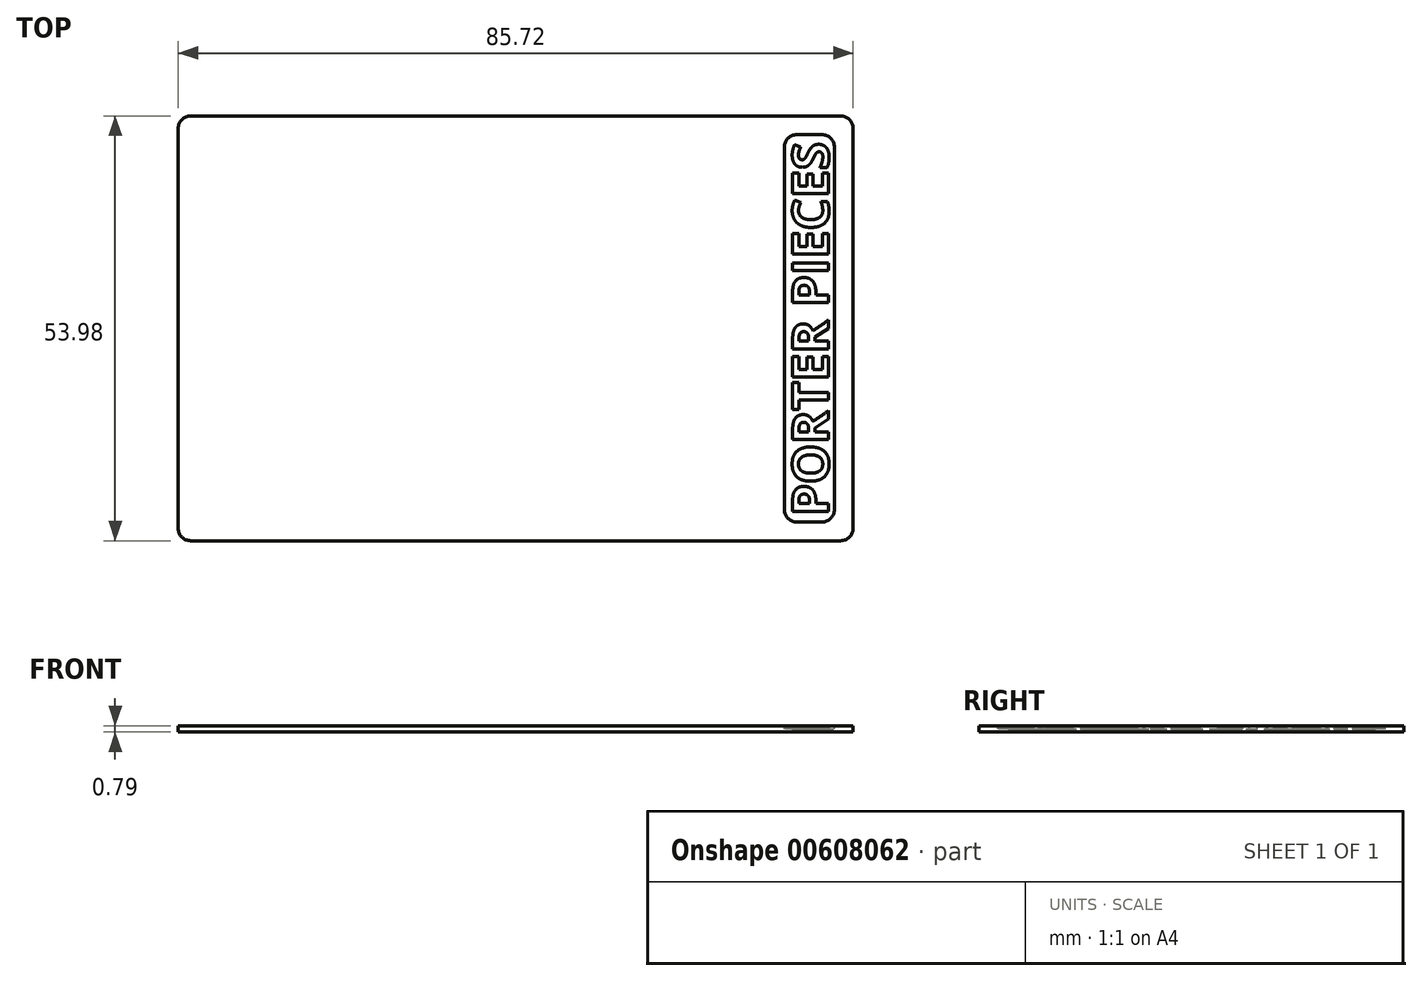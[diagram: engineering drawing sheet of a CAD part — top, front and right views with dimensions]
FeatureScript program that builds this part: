
annotation { "Feature Type Name" : "Feature", "Feature Type Description" : "" }
export const myFeature = defineFeature(function(context is Context, id is Id, definition is map)
    precondition{}
    {
        {
            var Q0;
            Q0=qCreatedBy(makeId("Top.planeOp"),FACE);
            var sketch = newSketch(context, id + "F0", { "sketchPlane" : qUnion([Q0])});
            skLineSegment(sketch, "E0.bottom", {"start": v(42.86, 26.99) * mm, "end": v(-42.86, 26.99) * mm});
            skLineSegment(sketch, "E0.top", {"start": v(42.86, -26.99) * mm, "end": v(-42.86, -26.99) * mm});
            skLineSegment(sketch, "E0.left", {"start": v(42.86, 26.99) * mm, "end": v(42.86, -26.99) * mm});
            skLineSegment(sketch, "E0.right", {"start": v(-42.86, 26.99) * mm, "end": v(-42.86, -26.99) * mm});
            skPoint(sketch, "E0.middle", {"position": v(0, 0) * mm});
            skSolve(sketch);
        }
        {
            var Q0;
            Q0=makeQuery(id+"F0.imprint","IMPRINT",FACE,{"disambiguationData":[TD([[makeQuery(id+"F0.imprint","IMPRINT",EDGE,{"derivedFrom":sQuery(id+"F0.wireOp",EDGE,"E0.bottom")}),1.0]])]});
            extrude(context, id + "F1", {"entities" : qUnion([Q0]), "depth" : 0.8 * mm, "offsetDistance" : 25.4 * mm});
        }
        {
            var Q0;
            Q0=makeQuery(id+"F1.opExtrude","SWEPT_EDGE",EDGE,{"disambiguationData":[OSD([sQuery(id+"F0.wireOp",EDGE,"E0.bottom"),sQuery(id+"F0.wireOp",EDGE,"E0.left")])]});
            var Q1;
            Q1=makeQuery(id+"F1.opExtrude","SWEPT_EDGE",EDGE,{"disambiguationData":[OSD([sQuery(id+"F0.wireOp",EDGE,"E0.bottom"),sQuery(id+"F0.wireOp",EDGE,"E0.right")])]});
            var Q2;
            Q2=makeQuery(id+"F1.opExtrude","SWEPT_EDGE",EDGE,{"disambiguationData":[OSD([sQuery(id+"F0.wireOp",EDGE,"E0.top"),sQuery(id+"F0.wireOp",EDGE,"E0.right")])]});
            var Q3;
            Q3=makeQuery(id+"F1.opExtrude","SWEPT_EDGE",EDGE,{"disambiguationData":[OSD([sQuery(id+"F0.wireOp",EDGE,"E0.top"),sQuery(id+"F0.wireOp",EDGE,"E0.left")])]});
            fillet(context, id + "F2", {"entities" : qUnion([Q0, Q1, Q2, Q3]), "radius" : 1.59 * mm, "tangentPropagation" : true, "allowEdgeOverflow" : false});
        }
        {
            var Q0;
            Q0=makeQuery(id+"F1.opExtrude","CAP_FACE",FACE,{"disambiguationData":[OSD([sQuery(id+"F0.wireOp",EDGE,"E0.bottom"),sQuery(id+"F0.wireOp",EDGE,"E0.top"),sQuery(id+"F0.wireOp",EDGE,"E0.left"),sQuery(id+"F0.wireOp",EDGE,"E0.right")])],"isStart":false});
            var sketch = newSketch(context, id + "F3", { "sketchPlane" : qUnion([Q0])});
            skLineSegment(sketch, "E1.bottom", {"start": v(34.13, -24.6) * mm, "end": v(40.48, -24.6) * mm});
            skLineSegment(sketch, "E1.top", {"start": v(34.13, 24.6) * mm, "end": v(40.48, 24.6) * mm});
            skLineSegment(sketch, "E1.left", {"start": v(34.13, -24.6) * mm, "end": v(34.13, 24.6) * mm});
            skLineSegment(sketch, "E1.right", {"start": v(40.48, -24.6) * mm, "end": v(40.48, 24.6) * mm});
            skSolve(sketch);
        }
        {
            var Q0;
            Q0=makeQuery(id+"F3.imprint","IMPRINT",FACE,{"disambiguationData":[TD([[makeQuery(id+"F3.imprint","IMPRINT",EDGE,{"derivedFrom":sQuery(id+"F3.wireOp",EDGE,"E1.bottom")}),1.0]])]});
            extrude(context, id + "F4", {"entities" : qUnion([Q0]), "operationType" : NewBodyOperationType.REMOVE, "oppositeDirection" : true, "depth" : 0.4 * mm, "offsetDistance" : 25.4 * mm});
        }
        {
            var Q0;
            Q0=makeQuery(id+"F4.boolean.opBoolean","COPY",EDGE,{"derivedFrom":makeQuery(id+"F4.opExtrude","SWEPT_EDGE",EDGE,{"disambiguationData":[OSD([sQuery(id+"F3.wireOp",EDGE,"E1.bottom"),sQuery(id+"F3.wireOp",EDGE,"E1.left")])]})});
            var Q1;
            Q1=makeQuery(id+"F4.boolean.opBoolean","COPY",EDGE,{"derivedFrom":makeQuery(id+"F4.opExtrude","SWEPT_EDGE",EDGE,{"disambiguationData":[OSD([sQuery(id+"F3.wireOp",EDGE,"E1.bottom"),sQuery(id+"F3.wireOp",EDGE,"E1.right")])]})});
            var Q2;
            Q2=makeQuery(id+"F4.boolean.opBoolean","COPY",EDGE,{"derivedFrom":makeQuery(id+"F4.opExtrude","SWEPT_EDGE",EDGE,{"disambiguationData":[OSD([sQuery(id+"F3.wireOp",EDGE,"E1.top"),sQuery(id+"F3.wireOp",EDGE,"E1.right")])]})});
            var Q3;
            Q3=makeQuery(id+"F4.boolean.opBoolean","COPY",EDGE,{"derivedFrom":makeQuery(id+"F4.opExtrude","SWEPT_EDGE",EDGE,{"disambiguationData":[OSD([sQuery(id+"F3.wireOp",EDGE,"E1.top"),sQuery(id+"F3.wireOp",EDGE,"E1.left")])]})});
            fillet(context, id + "F5", {"entities" : qUnion([Q0, Q1, Q2, Q3]), "radius" : 1.59 * mm, "tangentPropagation" : true, "allowEdgeOverflow" : false});
        }
        {
            var Q0;
            Q0=makeQuery(id+"F4.boolean.opBoolean","COPY",FACE,{"derivedFrom":makeQuery(id+"F4.opExtrude","CAP_FACE",FACE,{"disambiguationData":[OSD([sQuery(id+"F3.wireOp",EDGE,"E1.bottom"),sQuery(id+"F3.wireOp",EDGE,"E1.top"),sQuery(id+"F3.wireOp",EDGE,"E1.left"),sQuery(id+"F3.wireOp",EDGE,"E1.right")])],"isStart":false})});
            var sketch = newSketch(context, id + "F6", { "sketchPlane" : qUnion([Q0])});
            skText(sketch, "E2", { "text": "PORTER PIECES", "fontName": "OpenSans-Bold.ttf"});
            const initialGuessF6  = {"E2": [0.03976, -0.02381, 0, 1, 0.00461]};
            skSetInitialGuess(sketch, initialGuessF6);
            skSolve(sketch);
        }
        {
            var Q0;
            Q0=makeQuery(id+"F6.imprint","IMPRINT",FACE,{"disambiguationData":[TD([[makeQuery(id+"F6.imprint","IMPRINT",EDGE,{"derivedFrom":sQuery(id+"F6.wireOp",EDGE,"E2.sketch_text.stroke-0")}),-1.0]])]});
            var Q1;
            Q1=makeQuery(id+"F6.imprint","IMPRINT",FACE,{"disambiguationData":[TD([[makeQuery(id+"F6.imprint","IMPRINT",EDGE,{"derivedFrom":sQuery(id+"F6.wireOp",EDGE,"E2.sketch_text.stroke-16")}),-1.0]])]});
            var Q2;
            Q2=makeQuery(id+"F6.imprint","IMPRINT",FACE,{"disambiguationData":[TD([[makeQuery(id+"F6.imprint","IMPRINT",EDGE,{"derivedFrom":sQuery(id+"F6.wireOp",EDGE,"E2.sketch_text.stroke-30")}),-1.0]])]});
            var Q3;
            Q3=makeQuery(id+"F6.imprint","IMPRINT",FACE,{"disambiguationData":[TD([[makeQuery(id+"F6.imprint","IMPRINT",EDGE,{"derivedFrom":sQuery(id+"F6.wireOp",EDGE,"E2.sketch_text.stroke-49")}),-1.0]])]});
            var Q4;
            Q4=makeQuery(id+"F6.imprint","IMPRINT",FACE,{"disambiguationData":[TD([[makeQuery(id+"F6.imprint","IMPRINT",EDGE,{"derivedFrom":sQuery(id+"F6.wireOp",EDGE,"E2.sketch_text.stroke-57")}),-1.0]])]});
            var Q5;
            Q5=makeQuery(id+"F6.imprint","IMPRINT",FACE,{"disambiguationData":[TD([[makeQuery(id+"F6.imprint","IMPRINT",EDGE,{"derivedFrom":sQuery(id+"F6.wireOp",EDGE,"E2.sketch_text.stroke-69")}),-1.0]])]});
            var Q6;
            Q6=makeQuery(id+"F6.imprint","IMPRINT",FACE,{"disambiguationData":[TD([[makeQuery(id+"F6.imprint","IMPRINT",EDGE,{"derivedFrom":sQuery(id+"F6.wireOp",EDGE,"E2.sketch_text.stroke-88")}),-1.0]])]});
            var Q7;
            Q7=makeQuery(id+"F6.imprint","IMPRINT",FACE,{"disambiguationData":[TD([[makeQuery(id+"F6.imprint","IMPRINT",EDGE,{"derivedFrom":sQuery(id+"F6.wireOp",EDGE,"E2.sketch_text.stroke-104")}),-1.0]])]});
            var Q8;
            Q8=makeQuery(id+"F6.imprint","IMPRINT",FACE,{"disambiguationData":[TD([[makeQuery(id+"F6.imprint","IMPRINT",EDGE,{"derivedFrom":sQuery(id+"F6.wireOp",EDGE,"E2.sketch_text.stroke-108")}),-1.0]])]});
            var Q9;
            Q9=makeQuery(id+"F6.imprint","IMPRINT",FACE,{"disambiguationData":[TD([[makeQuery(id+"F6.imprint","IMPRINT",EDGE,{"derivedFrom":sQuery(id+"F6.wireOp",EDGE,"E2.sketch_text.stroke-120")}),-1.0]])]});
            var Q10;
            Q10=makeQuery(id+"F6.imprint","IMPRINT",FACE,{"disambiguationData":[TD([[makeQuery(id+"F6.imprint","IMPRINT",EDGE,{"derivedFrom":sQuery(id+"F6.wireOp",EDGE,"E2.sketch_text.stroke-135")}),-1.0]])]});
            var Q11;
            Q11=makeQuery(id+"F6.imprint","IMPRINT",FACE,{"disambiguationData":[TD([[makeQuery(id+"F6.imprint","IMPRINT",EDGE,{"derivedFrom":sQuery(id+"F6.wireOp",EDGE,"E2.sketch_text.stroke-147")}),-1.0]])]});
            extrude(context, id + "F7", {"entities" : qUnion([Q0, Q1, Q2, Q3, Q4, Q5, Q6, Q7, Q8, Q9, Q10, Q11]), "operationType" : NewBodyOperationType.ADD, "depth" : 0.4 * mm, "offsetDistance" : 25.4 * mm});
        }
    });
